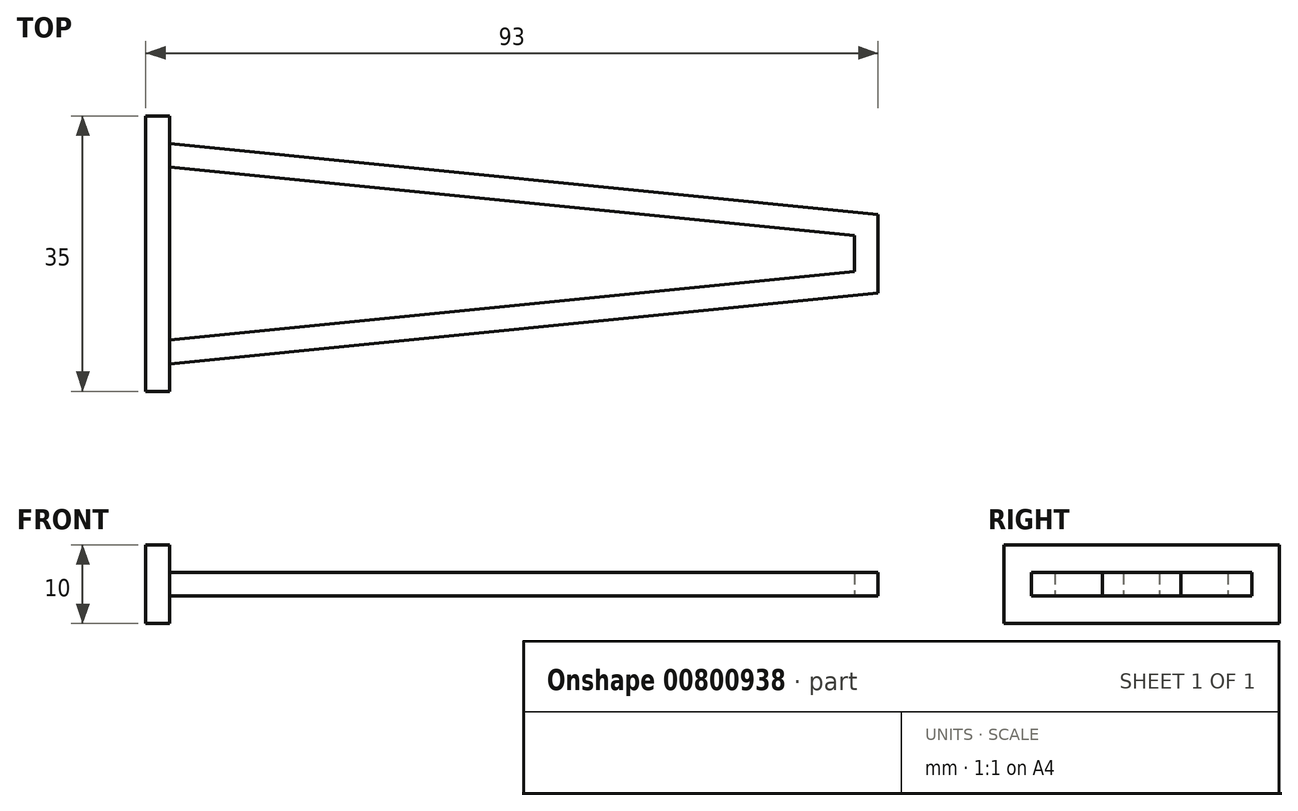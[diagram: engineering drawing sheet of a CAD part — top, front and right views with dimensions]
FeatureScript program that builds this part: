
annotation { "Feature Type Name" : "Feature", "Feature Type Description" : "" }
export const myFeature = defineFeature(function(context is Context, id is Id, definition is map)
    precondition{}
    {
        {
            var Q0;
            Q0=qCreatedBy(makeId("Right.planeOp"),FACE);
            var sketch = newSketch(context, id + "F0", { "sketchPlane" : qUnion([Q0])});
            skLineSegment(sketch, "E0.bottom", {"start": v(17.5, 5) * mm, "end": v(-17.5, 5) * mm});
            skLineSegment(sketch, "E0.top", {"start": v(17.5, -5) * mm, "end": v(-17.5, -5) * mm});
            skLineSegment(sketch, "E0.left", {"start": v(17.5, 5) * mm, "end": v(17.5, -5) * mm});
            skLineSegment(sketch, "E0.right", {"start": v(-17.5, 5) * mm, "end": v(-17.5, -5) * mm});
            skPoint(sketch, "E0.middle", {"position": v(0, 0) * mm});
            skSolve(sketch);
        }
        {
            var Q0;
            Q0 = qSketchRegion(id + "F0", true);
            extrude(context, id + "F1", {"entities" : qUnion([Q0]), "depth" : 3 * mm, "offsetDistance" : 25 * mm});
        }
        {
            var Q0;
            Q0=qCreatedBy(makeId("Top.planeOp"),FACE);
            var sketch = newSketch(context, id + "F2", { "sketchPlane" : qUnion([Q0])});
            skLineSegment(sketch, "E1", {"start": v(3, -14) * mm, "end": v(93, -5) * mm});
            skLineSegment(sketch, "E2", {"start": v(93, -5) * mm, "end": v(93, 5) * mm});
            skLineSegment(sketch, "E3", {"start": v(93, 5) * mm, "end": v(3, 14) * mm});
            skLineSegment(sketch, "E4", {"start": v(3, 14) * mm, "end": v(3, 10.99) * mm});
            skLineSegment(sketch, "E5", {"start": v(-12.79, 0) * mm, "end": v(-5.08, 0) * mm, "construction": true});
            skLineSegment(sketch, "E6.0", {"start": v(3, -10.99) * mm, "end": v(90, -2.29) * mm});
            skLineSegment(sketch, "E6.2", {"start": v(90, 2.29) * mm, "end": v(3, 10.99) * mm});
            skLineSegment(sketch, "E6.3", {"start": v(90, -2.29) * mm, "end": v(90, 2.29) * mm});
            skLineSegment(sketch, "E7.trimOffspring", {"start": v(3, -10.99) * mm, "end": v(3, -14) * mm});
            skSolve(sketch);
        }
        {
            var Q0;
            Q0=makeQuery(id+"F2.imprint","IMPRINT",FACE,{"disambiguationData":[TD([[makeQuery(id+"F2.imprint","IMPRINT",EDGE,{"derivedFrom":sQuery(id+"F2.wireOp",EDGE,"E1")}),1.0]])]});
            extrude(context, id + "F3", {"entities" : qUnion([Q0]), "operationType" : NewBodyOperationType.ADD, "endBound" : BoundingType.SYMMETRIC, "depth" : 3 * mm, "offsetDistance" : 25 * mm});
        }
    });
